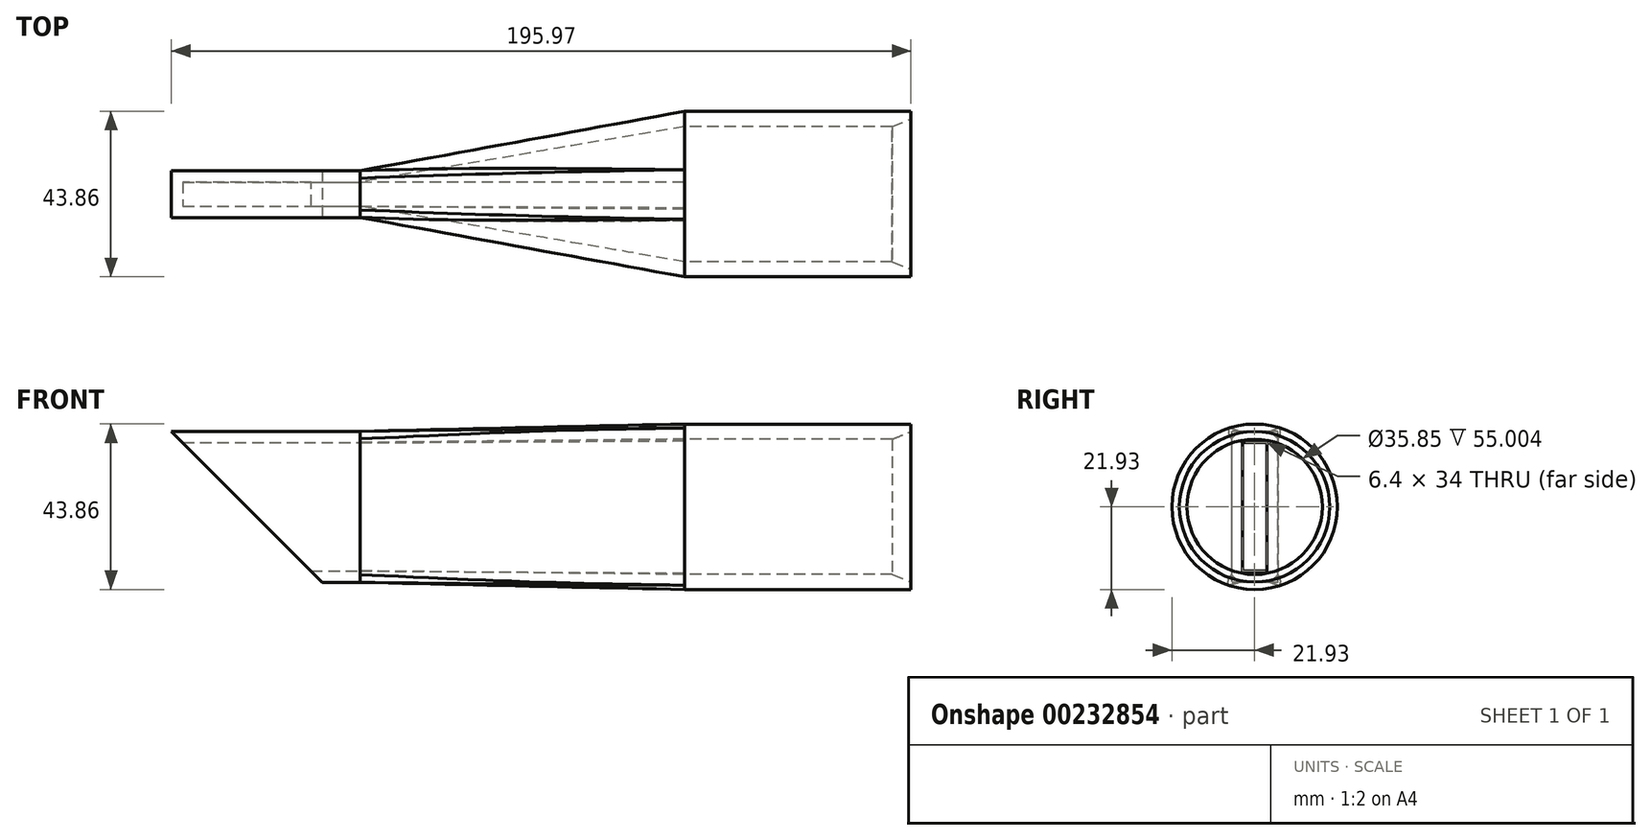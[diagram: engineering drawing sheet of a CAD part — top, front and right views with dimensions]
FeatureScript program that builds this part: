
annotation { "Feature Type Name" : "Feature", "Feature Type Description" : "" }
export const myFeature = defineFeature(function(context is Context, id is Id, definition is map)
    precondition{}
    {
        {
            var Q0;
            Q0=qCreatedBy(makeId("Front.planeOp"),FACE);
            var sketch = newSketch(context, id + "F0", { "sketchPlane" : qUnion([Q0])});
            skLineSegment(sketch, "E0", {"start": v(-54.03, 0) * mm, "end": v(-4.03, 0) * mm, "construction": true});
            skLineSegment(sketch, "E1", {"start": v(-4.03, 0) * mm, "end": v(-4.03, 17.93) * mm, "construction": true});
            skLineSegment(sketch, "E2", {"start": v(-54.04, 0.55) * mm, "end": v(-54.04, 17.93) * mm, "construction": true});
            skLineSegment(sketch, "E3", {"start": v(-54.04, 17.92) * mm, "end": v(5.97, 17.93) * mm});
            skLineSegment(sketch, "E4", {"start": v(-54.04, 17.93) * mm, "end": v(-54.04, 21.92) * mm});
            skLineSegment(sketch, "E5", {"start": v(5.97, 17.93) * mm, "end": v(5.97, 21.93) * mm});
            skLineSegment(sketch, "E6", {"start": v(5.97, 21.93) * mm, "end": v(-54.04, 21.92) * mm});
            skSolve(sketch);
        }
        {
            var Q0;
            Q0=makeQuery(id+"F0.imprint","IMPRINT",FACE,{"disambiguationData":[TD([[makeQuery(id+"F0.imprint","IMPRINT",EDGE,{"derivedFrom":sQuery(id+"F0.wireOp",EDGE,"E3")}),1.0]])]});
            var Q1;
            Q1=sQuery(id+"F0.wireOp",EDGE,"E0");
            revolve(context, id + "F1", {"entities" : qUnion([Q0]), "axis" : qUnion([Q1]), "revolveType" : RevolveType.FULL});
        }
        {
            var Q0;
            Q0=makeQuery(id+"F1.opRevolve","SWEPT_EDGE",EDGE,{"disambiguationData":[OSD([sQuery(id+"F0.wireOp",EDGE,"E3"),sQuery(id+"F0.wireOp",EDGE,"E5")])]});
            chamfer(context, id + "F2", {"entities" : qUnion([Q0]), "chamferType" : ChamferType.TWO_OFFSETS, "width1" : 2 * mm, "oppositeDirection" : false, "width2" : 5 * mm, "tangentPropagation" : true});
        }
        {
            var Q0;
            Q0=qCreatedBy(makeId("Right.planeOp"),FACE);
            cPlane(context, id + "F3", {"entities" : qUnion([Q0]), "cplaneType" : CPlaneType.OFFSET, "offset" : 140 * mm, "oppositeDirection" : true, "width" : 150 * mm, "height" : 150 * mm});
        }
        {
            var Q0;
            Q0=qCreatedBy(id+"F3.planeOp",FACE);
            var sketch = newSketch(context, id + "F4", { "sketchPlane" : qUnion([Q0])});
            skPoint(sketch, "E7.0", {"position": v(0, 0) * mm});
            skLineSegment(sketch, "E8.bottom", {"start": v(6.2, 20) * mm, "end": v(-6.2, 20) * mm});
            skLineSegment(sketch, "E8.top", {"start": v(6.2, -20) * mm, "end": v(-6.2, -20) * mm});
            skLineSegment(sketch, "E8.left", {"start": v(6.2, 20) * mm, "end": v(6.2, -20) * mm});
            skLineSegment(sketch, "E8.right", {"start": v(-6.2, 20) * mm, "end": v(-6.2, -20) * mm});
            skLineSegment(sketch, "E9.0", {"start": v(3.2, 17) * mm, "end": v(-3.2, 17) * mm});
            skLineSegment(sketch, "E9.1", {"start": v(3.2, 17) * mm, "end": v(3.2, -17) * mm});
            skLineSegment(sketch, "E9.2", {"start": v(3.2, -17) * mm, "end": v(-3.2, -17) * mm});
            skLineSegment(sketch, "E9.3", {"start": v(-3.2, 17) * mm, "end": v(-3.2, -17) * mm});
            skSolve(sketch);
        }
        {
            var Q0;
            Q0=makeQuery(id+"F1.opRevolve","SWEPT_FACE",FACE,{"disambiguationData":[OSD([sQuery(id+"F0.wireOp",EDGE,"E4")])]});
            var sketch = newSketch(context, id + "F5", { "sketchPlane" : qUnion([Q0])});
            skArc(sketch, "E10", {"start": v(-6.45, 20.96) * mm, "mid": v(-21.92, 0.06) * mm, "end": v(-6.57, -20.92) * mm});
            skArc(sketch, "E11", {"start": v(6.7, 20.88) * mm, "mid": v(0.13, 21.92) * mm, "end": v(-6.45, 20.96) * mm});
            skArc(sketch, "E12", {"start": v(-6.57, -20.92) * mm, "mid": v(0.26, -21.92) * mm, "end": v(7.06, -20.76) * mm});
            skArc(sketch, "E13", {"start": v(7.06, -20.76) * mm, "mid": v(21.92, 0.2) * mm, "end": v(6.7, 20.88) * mm});
            skArc(sketch, "E14", {"start": v(3.93, 17.49) * mm, "mid": v(0.31, 17.92) * mm, "end": v(-3.32, 17.62) * mm});
            skArc(sketch, "E15", {"start": v(-3.32, 17.62) * mm, "mid": v(-17.92, -0.02) * mm, "end": v(-3.28, -17.62) * mm});
            skArc(sketch, "E16", {"start": v(-3.28, -17.62) * mm, "mid": v(0.15, -17.92) * mm, "end": v(3.57, -17.57) * mm});
            skArc(sketch, "E17", {"start": v(3.57, -17.57) * mm, "mid": v(17.92, -0.19) * mm, "end": v(3.93, 17.49) * mm});
            skSolve(sketch);
        }
        {
            var Q0;
            Q0=makeQuery(id+"F4.imprint","IMPRINT",FACE,{"disambiguationData":[TD([[makeQuery(id+"F4.imprint","IMPRINT",EDGE,{"derivedFrom":sQuery(id+"F4.wireOp",EDGE,"E9.0")}),1.0]])]});
            var Q1;
            Q1=makeQuery(id+"F5.imprint","IMPRINT",FACE,{"disambiguationData":[TD([[makeQuery(id+"F5.imprint","IMPRINT",EDGE,{"derivedFrom":sQuery(id+"F5.wireOp",EDGE,"E14")}),1.0]])]});
            loft(context, id + "F6", {"sheetProfilesArray" : [{ "sheetProfileEntities" : qUnion([Q0]) }, { "sheetProfileEntities" : qUnion([Q1]) }]});
        }
        {
            var Q0;
            Q0=qCreatedBy(id+"F3.planeOp",FACE);
            var sketch = newSketch(context, id + "F7", { "sketchPlane" : qUnion([Q0])});
            skLineSegment(sketch, "E18.0", {"start": v(6.2, 20) * mm, "end": v(-6.2, 20) * mm});
            skLineSegment(sketch, "E19.0", {"start": v(6.2, 20) * mm, "end": v(6.2, -20) * mm});
            skLineSegment(sketch, "E20.0", {"start": v(-6.2, 20) * mm, "end": v(-6.2, -20) * mm});
            skLineSegment(sketch, "E21.0", {"start": v(6.2, -20) * mm, "end": v(-6.2, -20) * mm});
            skSolve(sketch);
        }
        {
            var Q0;
            Q0=makeQuery(id+"F5.imprint","IMPRINT",FACE,{"disambiguationData":[TD([[makeQuery(id+"F5.imprint","IMPRINT",EDGE,{"derivedFrom":sQuery(id+"F5.wireOp",EDGE,"E14")}),1.0]])]});
            var sketch = newSketch(context, id + "F8", { "sketchPlane" : qUnion([Q0])});
            skArc(sketch, "E22.0", {"start": v(-6.45, 20.96) * mm, "mid": v(-21.92, 0.06) * mm, "end": v(-6.57, -20.92) * mm});
            skArc(sketch, "E23.0", {"start": v(6.7, 20.88) * mm, "mid": v(0.13, 21.92) * mm, "end": v(-6.45, 20.96) * mm});
            skArc(sketch, "E24.0", {"start": v(7.06, -20.76) * mm, "mid": v(21.92, 0.2) * mm, "end": v(6.7, 20.88) * mm});
            skArc(sketch, "E25.0", {"start": v(-6.57, -20.92) * mm, "mid": v(0.26, -21.92) * mm, "end": v(7.06, -20.76) * mm});
            skSolve(sketch);
        }
        {
            var Q1;
            Q1=makeQuery(id+"F7.imprint","IMPRINT",FACE,{"disambiguationData":[TD([[makeQuery(id+"F7.imprint","IMPRINT",EDGE,{"derivedFrom":sQuery(id+"F7.wireOp",EDGE,"E18.0")}),1.0]])]});
            var Q2;
            Q2=qSketchRegion(id+"F8",true);
            loft(context, id + "F9", {"sheetProfilesArray" : [{ "sheetProfileEntities" : qUnion([Q1]) }, { "sheetProfileEntities" : qUnion([Q2]) }]});
        }
        {
            var Q0;
            Q0=makeQuery(id+"F6.opLoft","SWEPT_BODY",BODY,{"disambiguationData":[OSD([makeQuery(id+"F4.imprint","IMPRINT",FACE,{"disambiguationData":[TD([[makeQuery(id+"F4.imprint","IMPRINT",EDGE,{"derivedFrom":sQuery(id+"F4.wireOp",EDGE,"E9.0")}),1.0]])]}),makeQuery(id+"F5.imprint","IMPRINT",FACE,{"disambiguationData":[TD([[makeQuery(id+"F5.imprint","IMPRINT",EDGE,{"derivedFrom":sQuery(id+"F5.wireOp",EDGE,"E14")}),1.0]])]})])]});
            var Q1;
            Q1=makeQuery(id+"F9.opLoft","SWEPT_BODY",BODY,{"disambiguationData":[OSD([makeQuery(id+"F7.imprint","IMPRINT",FACE,{"disambiguationData":[TD([[makeQuery(id+"F7.imprint","IMPRINT",EDGE,{"derivedFrom":sQuery(id+"F7.wireOp",EDGE,"E18.0")}),1.0]])]}),makeQuery(id+"F8.imprint","IMPRINT",FACE,{"disambiguationData":[TD([[makeQuery(id+"F8.imprint","IMPRINT",EDGE,{"derivedFrom":sQuery(id+"F8.wireOp",EDGE,"E22.0")}),1.0]])]})])]});
            booleanBodies(context, id + "F10", {"operationType" : BooleanOperationType.SUBTRACTION, "tools" : qUnion([Q0]), "targets" : qUnion([Q1])});
        }
        {
            var Q0;
            Q0=makeQuery(id+"F9.opLoft","CAP_FACE",FACE,{"disambiguationData":[OSD([makeQuery(id+"F7.imprint","IMPRINT",FACE,{"disambiguationData":[TD([[makeQuery(id+"F7.imprint","IMPRINT",EDGE,{"derivedFrom":sQuery(id+"F7.wireOp",EDGE,"E18.0")}),1.0]])]})])],"isStart":true});
            extrude(context, id + "F11", {"entities" : qUnion([Q0]), "depth" : 50 * mm});
        }
        {
            var Q0;
            Q0=makeQuery(id+"F11.opExtrude","SWEPT_FACE",FACE,{"disambiguationData":[OSD([sQuery(id+"F7.wireOp",EDGE,"E18.0"),sQuery(id+"F7.wireOp",EDGE,"E20.0"),sQuery(id+"F7.wireOp",EDGE,"E21.0")])]});
            var sketch = newSketch(context, id + "F12", { "sketchPlane" : qUnion([Q0])});
            skLineSegment(sketch, "E26.0", {"start": v(-190, 20) * mm, "end": v(-190, -20) * mm});
            skFitSpline(sketch, "E27.0", {"points": [v(-210, 20) * mm, v(-193.33, 20) * mm, v(-176.67, 20) * mm, v(-160, 20) * mm]});
            skFitSpline(sketch, "E28.0", {"points": [v(-210, -20) * mm, v(-193.33, -20) * mm, v(-176.67, -20) * mm, v(-160, -20) * mm]});
            skLineSegment(sketch, "E29", {"start": v(-190, 20) * mm, "end": v(-150, -20) * mm});
            skSolve(sketch);
        }
        {
            var Q0;
            {var subQ0=sQuery(id+"F12.wireOp",EDGE,"E26.0");Q0=makeQuery(id+"F12.imprint","IMPRINT",FACE,{"disambiguationData":[TD([[makeQuery(id+"F12.imprint","IMPRINT",EDGE,{"derivedFrom":subQ0}),1.0]])]});}
            extrude(context, id + "F13", {"entities" : qUnion([Q0]), "operationType" : NewBodyOperationType.REMOVE, "endBound" : BoundingType.SYMMETRIC, "oppositeDirection" : true, "depth" : 25 * mm});
        }
        {
            var Q0;
            Q0=makeQuery(id+"F13.boolean.opBoolean","MERGE",EDGE,{"derivedFrom":[makeQuery(id+"F11.opExtrude","CAP_EDGE",EDGE,{"disambiguationData":[OSD([sQuery(id+"F7.wireOp",EDGE,"E18.0"),sQuery(id+"F7.wireOp",EDGE,"E19.0"),sQuery(id+"F7.wireOp",EDGE,"E20.0")])],"isStart":false}),makeQuery(id+"F13.opExtrude","SWEPT_EDGE",EDGE,{"disambiguationData":[OSD([sQuery(id+"F12.wireOp",EDGE,"E26.0"),sQuery(id+"F12.wireOp",EDGE,"E27.0"),sQuery(id+"F12.wireOp",EDGE,"E29")])]})]});
            var Q1;
            Q1=makeQuery(id+"F13.boolean.opBoolean","INTERSECT",EDGE,{"derivedFrom":[makeQuery(id+"F11.opExtrude","SWEPT_FACE",FACE,{"disambiguationData":[OSD([sQuery(id+"F7.wireOp",EDGE,"E18.0"),sQuery(id+"F7.wireOp",EDGE,"E19.0"),sQuery(id+"F7.wireOp",EDGE,"E21.0")])]}),makeQuery(id+"F13.opExtrude","SWEPT_FACE",FACE,{"disambiguationData":[OSD([sQuery(id+"F12.wireOp",EDGE,"E29")])]})]});
            var Q2;
            Q2=makeQuery(id+"F13.boolean.opBoolean","COPY",EDGE,{"derivedFrom":makeQuery(id+"F13.opExtrude","SWEPT_EDGE",EDGE,{"disambiguationData":[OSD([sQuery(id+"F12.wireOp",EDGE,"E28.0"),sQuery(id+"F12.wireOp",EDGE,"E29")])]})});
            var Q3;
            Q3=makeQuery(id+"F13.boolean.opBoolean","INTERSECT",EDGE,{"derivedFrom":[makeQuery(id+"F11.opExtrude","SWEPT_FACE",FACE,{"disambiguationData":[OSD([sQuery(id+"F7.wireOp",EDGE,"E18.0"),sQuery(id+"F7.wireOp",EDGE,"E20.0"),sQuery(id+"F7.wireOp",EDGE,"E21.0")])]}),makeQuery(id+"F13.opExtrude","SWEPT_FACE",FACE,{"disambiguationData":[OSD([sQuery(id+"F12.wireOp",EDGE,"E29")])]})]});
            var Q4;
            Q4=makeQuery(id+"F13.boolean.opBoolean","INTERSECT",EDGE,{"derivedFrom":[makeQuery(id+"F11.opExtrude","SWEPT_FACE",FACE,{"disambiguationData":[OSD([sQuery(id+"F4.wireOp",EDGE,"E9.0"),sQuery(id+"F4.wireOp",EDGE,"E9.1"),sQuery(id+"F4.wireOp",EDGE,"E9.2")])]}),makeQuery(id+"F13.opExtrude","SWEPT_FACE",FACE,{"disambiguationData":[OSD([sQuery(id+"F12.wireOp",EDGE,"E29")])]})]});
            var Q5;
            Q5=makeQuery(id+"F13.boolean.opBoolean","INTERSECT",EDGE,{"derivedFrom":[makeQuery(id+"F11.opExtrude","SWEPT_FACE",FACE,{"disambiguationData":[OSD([sQuery(id+"F4.wireOp",EDGE,"E9.0"),sQuery(id+"F4.wireOp",EDGE,"E9.1"),sQuery(id+"F4.wireOp",EDGE,"E9.3")])]}),makeQuery(id+"F13.opExtrude","SWEPT_FACE",FACE,{"disambiguationData":[OSD([sQuery(id+"F12.wireOp",EDGE,"E29")])]})]});
            var Q6;
            Q6=makeQuery(id+"F13.boolean.opBoolean","INTERSECT",EDGE,{"derivedFrom":[makeQuery(id+"F11.opExtrude","SWEPT_FACE",FACE,{"disambiguationData":[OSD([sQuery(id+"F4.wireOp",EDGE,"E9.0"),sQuery(id+"F4.wireOp",EDGE,"E9.2"),sQuery(id+"F4.wireOp",EDGE,"E9.3")])]}),makeQuery(id+"F13.opExtrude","SWEPT_FACE",FACE,{"disambiguationData":[OSD([sQuery(id+"F12.wireOp",EDGE,"E29")])]})]});
            var Q7;
            Q7=makeQuery(id+"F13.boolean.opBoolean","INTERSECT",EDGE,{"derivedFrom":[makeQuery(id+"F11.opExtrude","SWEPT_FACE",FACE,{"disambiguationData":[OSD([sQuery(id+"F4.wireOp",EDGE,"E9.1"),sQuery(id+"F4.wireOp",EDGE,"E9.2"),sQuery(id+"F4.wireOp",EDGE,"E9.3")])]}),makeQuery(id+"F13.opExtrude","SWEPT_FACE",FACE,{"disambiguationData":[OSD([sQuery(id+"F12.wireOp",EDGE,"E29")])]})]});
            var Q8;
            Q8=makeQuery(id+"F11.opExtrude","SWEPT_EDGE",EDGE,{"disambiguationData":[OSD([sQuery(id+"F7.wireOp",EDGE,"E18.0"),sQuery(id+"F7.wireOp",EDGE,"E19.0")])]});
            var Q9;
            Q9=makeQuery(id+"F11.opExtrude","SWEPT_EDGE",EDGE,{"disambiguationData":[OSD([sQuery(id+"F7.wireOp",EDGE,"E18.0"),sQuery(id+"F7.wireOp",EDGE,"E20.0")])]});
            var Q10;
            Q10=makeQuery(id+"F11.opExtrude","SWEPT_EDGE",EDGE,{"disambiguationData":[OSD([sQuery(id+"F7.wireOp",EDGE,"E19.0"),sQuery(id+"F7.wireOp",EDGE,"E21.0")])]});
            var Q11;
            Q11=makeQuery(id+"F11.opExtrude","SWEPT_EDGE",EDGE,{"disambiguationData":[OSD([sQuery(id+"F7.wireOp",EDGE,"E20.0"),sQuery(id+"F7.wireOp",EDGE,"E21.0")])]});
            var Q12;
            Q12=makeQuery(id+"F9.opLoft","SWEPT_EDGE",EDGE,{"disambiguationData":[OSD([sQuery(id+"F7.wireOp",EDGE,"E19.0"),sQuery(id+"F7.wireOp",EDGE,"E21.0"),sQuery(id+"F8.wireOp",EDGE,"E22.0"),sQuery(id+"F8.wireOp",EDGE,"E25.0")])]});
            var Q13;
            Q13=makeQuery(id+"F9.opLoft","SWEPT_EDGE",EDGE,{"disambiguationData":[OSD([sQuery(id+"F7.wireOp",EDGE,"E20.0"),sQuery(id+"F7.wireOp",EDGE,"E21.0"),sQuery(id+"F8.wireOp",EDGE,"E24.0"),sQuery(id+"F8.wireOp",EDGE,"E25.0")])]});
            var Q14;
            Q14=makeQuery(id+"F9.opLoft","SWEPT_EDGE",EDGE,{"disambiguationData":[OSD([sQuery(id+"F7.wireOp",EDGE,"E18.0"),sQuery(id+"F7.wireOp",EDGE,"E19.0"),sQuery(id+"F8.wireOp",EDGE,"E22.0"),sQuery(id+"F8.wireOp",EDGE,"E23.0")])]});
            var Q15;
            Q15=makeQuery(id+"F9.opLoft","SWEPT_EDGE",EDGE,{"disambiguationData":[OSD([sQuery(id+"F7.wireOp",EDGE,"E18.0"),sQuery(id+"F7.wireOp",EDGE,"E20.0"),sQuery(id+"F8.wireOp",EDGE,"E23.0"),sQuery(id+"F8.wireOp",EDGE,"E24.0")])]});
            chamfer(context, id + "F14", {"entities" : qUnion([Q0, Q1, Q2, Q3, Q4, Q5, Q6, Q7, Q8, Q9, Q10, Q11, Q12, Q13, Q14, Q15]), "width" : 2 * mm, "tangentPropagation" : true});
        }
    });
